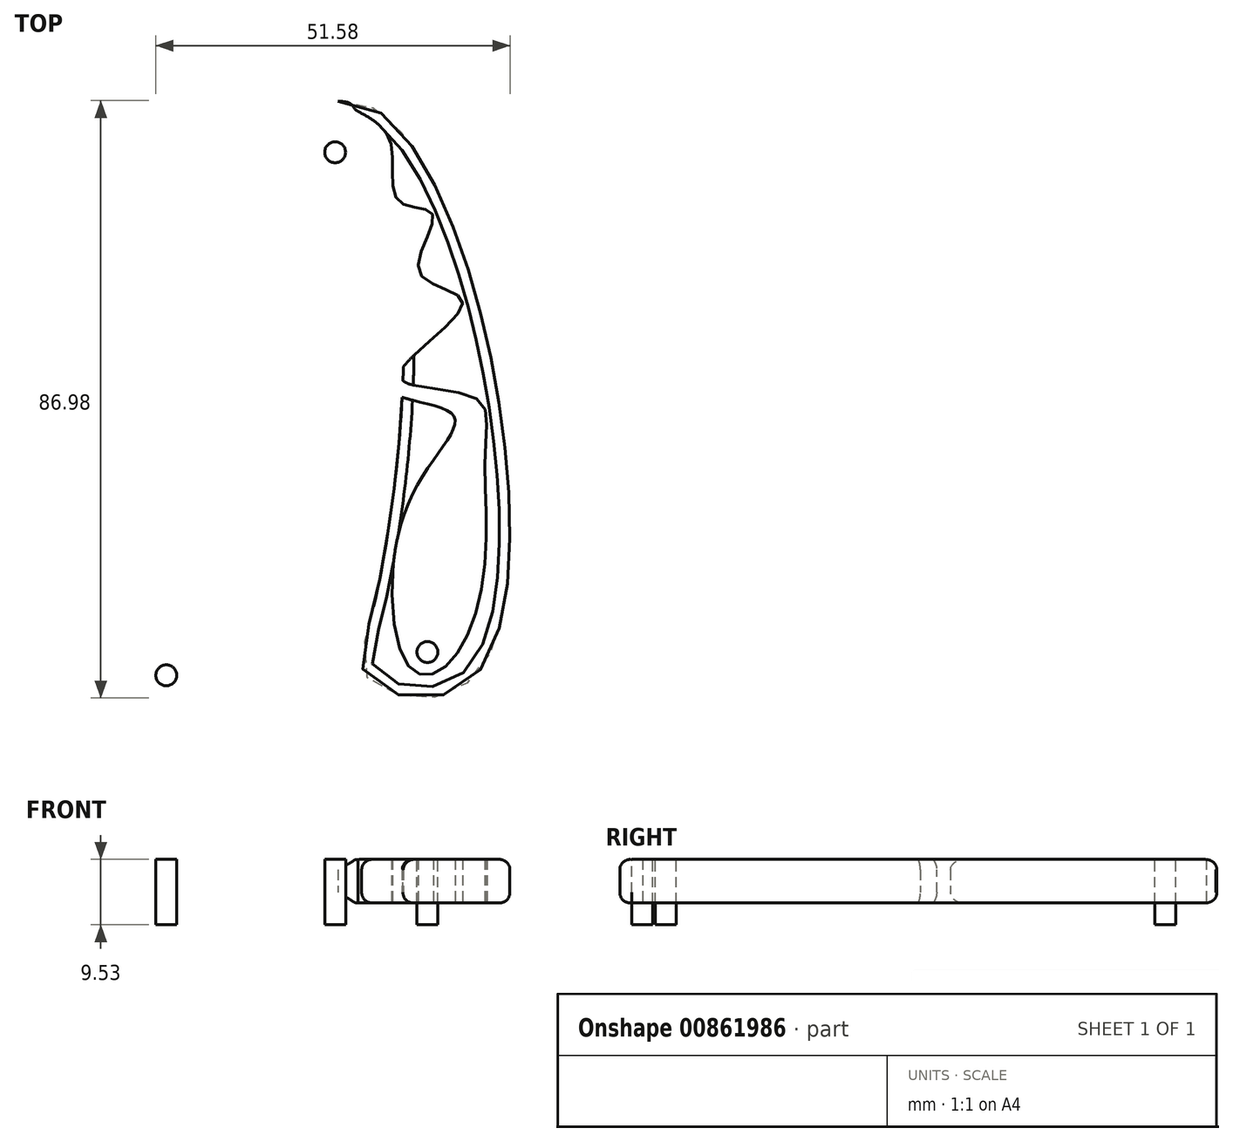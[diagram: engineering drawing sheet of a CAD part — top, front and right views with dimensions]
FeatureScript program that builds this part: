
annotation { "Feature Type Name" : "Feature", "Feature Type Description" : "" }
export const myFeature = defineFeature(function(context is Context, id is Id, definition is map)
    precondition{}
    {
        {
            var Q0;
            Q0=qCreatedBy(makeId("Top.planeOp"),FACE);
            var sketch = newSketch(context, id + "F0", { "sketchPlane" : qUnion([Q0])});
            skFitSpline(sketch, "E0", {"points": [v(-29.3, -33.01) * mm, v(-40.87, -31.24) * mm, v(-9.15, 53.1) * mm, v(11.22, -28.43) * mm, v(-5.55, -31.5) * mm, v(-5.06, -19.9) * mm, v(-4.35, 34.98) * mm, v(-19.43, 27.86) * mm, v(-30.03, -26.57) * mm, v(-29.3, -33.01) * mm]});
            skPoint(sketch, "E1.0.internal.snap0", {"position": v(-7.5, 43.13) * mm});
            skFitSpline(sketch, "E1", {"points": [v(-7.5, 51.57) * mm, v(-2.7, 46.92) * mm, v(-1.54, 38.5) * mm, v(3.4, 36.46) * mm, v(1.5, 28.03) * mm, v(7.76, 23.67) * mm, v(-1.4, 13.06) * mm, v(9.5, 9.86) * mm, v(11.06, 2.75) * mm, v(10.8, -16.22) * mm, v(4.92, -29.56) * mm, v(0, -29.38) * mm, v(0, -5.19) * mm, v(6.17, 7.55) * mm, v(-3.38, 11.71) * mm, v(5.5, 23.05) * mm, v(-1.14, 27.57) * mm, v(1.12, 35.06) * mm, v(-4.35, 34.98) * mm], "startDerivative": vector(140.08, -76.54) * mm, "endDerivative": vector(-79.22, 82.15) * mm});
            skFitSpline(sketch, "E2", {"points": [v(-10.4, 52.99) * mm, v(-7.5, 51.57) * mm], "startDerivative": vector(7.52, 0.36) * mm, "endDerivative": vector(2.64, -1.12) * mm});
            skCircle(sketch, "E3", {"center": v(-10.81, 45.6) * mm, "radius": 1.52 * mm});
            skCircle(sketch, "E4", {"center": v(2.64, -27.19) * mm, "radius": 1.52 * mm});
            skCircle(sketch, "E5", {"center": v(-35.4, -30.58) * mm, "radius": 1.52 * mm});
            skSolve(sketch);
        }
        {
            var Q0;
            {var subQ0=sQuery(id+"F0.wireOp",EDGE,"E0");Q0=makeQuery(id+"F0.imprint","IMPRINT",FACE,{"disambiguationData":[TD([[makeQuery(id+"F0.imprint","IMPRINT",EDGE,{"derivedFrom":subQ0}),-1.0]])]});}
            extrude(context, id + "F1", {"entities" : qUnion([Q0]), "endBound" : BoundingType.SYMMETRIC, "depth" : 6.35 * mm, "offsetDistance" : 25.4 * mm});
        }
        {
            var Q0;
            Q0=makeQuery(id+"F1.opExtrude","CAP_EDGE",EDGE,{"disambiguationData":[OSD([sQuery(id+"F0.wireOp",EDGE,"E0")])],"isStart":false});
            var Q1;
            Q1=makeQuery(id+"F1.opExtrude","CAP_EDGE",EDGE,{"disambiguationData":[OSD([sQuery(id+"F0.wireOp",EDGE,"E0")])],"isStart":true});
            fillet(context, id + "F2", {"entities" : qUnion([Q0, Q1]), "radius" : 1.52 * mm, "tangentPropagation" : true, "allowEdgeOverflow" : false});
        }
        {
            var Q0;
            Q0=makeQuery(id+"F0.imprint","IMPRINT",FACE,{"disambiguationData":[TD([[makeQuery(id+"F0.imprint","IMPRINT",EDGE,{"derivedFrom":sQuery(id+"F0.wireOp",EDGE,"E3")}),1.0]])]});
            var Q1;
            Q1=makeQuery(id+"F0.imprint","IMPRINT",FACE,{"disambiguationData":[TD([[makeQuery(id+"F0.imprint","IMPRINT",EDGE,{"derivedFrom":sQuery(id+"F0.wireOp",EDGE,"E5")}),1.0]])]});
            var Q2;
            Q2=makeQuery(id+"F0.imprint","IMPRINT",FACE,{"disambiguationData":[TD([[makeQuery(id+"F0.imprint","IMPRINT",EDGE,{"derivedFrom":sQuery(id+"F0.wireOp",EDGE,"E4")}),1.0]])]});
            var Q3;
            Q3=makeQuery(id+"F1.opExtrude","CAP_FACE",FACE,{"disambiguationData":[OSD([sQuery(id+"F0.wireOp",EDGE,"E0"),sQuery(id+"F0.wireOp",EDGE,"E1"),sQuery(id+"F0.wireOp",EDGE,"E2"),sQuery(id+"F0.wireOp",EDGE,"E3"),sQuery(id+"F0.wireOp",EDGE,"E4"),sQuery(id+"F0.wireOp",EDGE,"E5")])],"isStart":false});
            extrude(context, id + "F3", {"entities" : qUnion([Q0, Q1, Q2]), "operationType" : NewBodyOperationType.ADD, "oppositeDirection" : true, "depth" : 6.35 * mm, "offsetDistance" : 25.4 * mm, "hasSecondDirection" : true, "secondDirectionBound" : SecondDirectionBoundingType.UP_TO_SURFACE, "secondDirectionOppositeDirection" : false, "secondDirectionDepth" : 25.4 * mm, "secondDirectionBoundEntityFace" : qUnion([Q3])});
        }
    });
